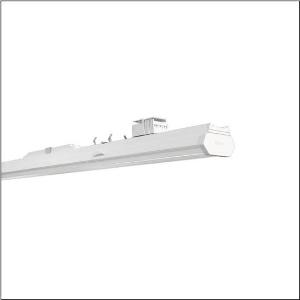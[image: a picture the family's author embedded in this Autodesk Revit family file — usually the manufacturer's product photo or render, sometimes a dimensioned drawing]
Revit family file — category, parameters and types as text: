
# Revit family: licross_r__11_protected_ho_51tp11mn4gxs_ec8e
name_source: partatom
category: Lighting Fixtures
units: mm (PartAtom-declared; Revit-internal decimal feet)

## family parameters
Cut with Voids When Loaded = No
Host = Face
Light Source = No
Part Type = Normal
Room Calculation Point = No
Round Connector Dimension = Use Diameter
Shared = No

## types (1)
- --- (1 x LED, 16070 lm, 87.4 W, 4000K)
    Apparent Load = 87 VA
    CIE Flux Codes = 84 94 98 99 100
    Color Rendering = 80
    Color Temperature = 4000K
    Default Elevation = 1800 mm
    Description = Licross® 11 Protected HO, luminaire insert, of sheet steel, galvanised, coil coated, white, length: 1.500mm, width: 90mm, height: 101mm, LED rated luminous flux: 16.070lm, light colour: 840, control gear: ON/OFF Multilumen, with plug, 3-pole, with phase selection, mains connection: 220..240V, AC, 50/60Hz, rated input power: 87W, halogen-free wiring, primary light control with lens, of plastic, primary optical cover: cover, of PMMA, light emission: direct distribution, primary light characteristic: symmetric, protection rating (complete): IP64, insulation class (complete): insulation class I (protective earthing), certification: CE, ENEC, VDE, UKCA, protection symbol: D if used in an environment with conductive dust loads with corresponding accessories, impact resistance: IK06, permissible ambient temperature for indoor applications: -35..+35°C, corresponds to IFS (International Featured Standards) requirements for safety and quality in the food industry, reducing of maximum allowable ambient temperature of 5°C with ceiling mounting, LABS conformity tested according to VDMA 24364:2018-05, packaging unit: 1 piece
    Height = 92 mm
    Lamp = 1 x LED
    Lamp Light Flux = 16070 lm
    Lamp Power = 87.4 W
    Lamp count = 1
    Length = 1500 mm
    Luminous efficacy = 184 lm/W
    Manufacturer = Siteco
    ModVariant = No
    Model = 51TP11MN4GXS
    Mounting Place = Ceiling
    Mounting Type = Pendant
    Number of Poles = 1
    OnlyDefault = Yes
    Power Factor = 1
    Product Name = Licross® 11 Protected HO
    Product group = luminaire insert
    ProductGroupID = 901
    Protection Class = Protection class I
    Protection Degree = IP 64
    RLX_Detail_Level = 1
    RLX_Emergency_Light_Flux = 0 lm
    RLX_Emergency_Type = 0
    RLX_Emergency_Type_DB = No
    RlxData = <blob elided: 22033 chars, md5=c27a27c4>
    Socket = socket
    Standby Power = 0 W
    System Light Flux = 16070 lm
    System Power = 87 W
    Type Comments = factory setting: luminous flux: 100 % | (A | C | E) | 203 mA
    Type Image = l_1256148.jpg
    URL = http://relux.com
    VarID = @adj_055203
    Voltage = 0 V
    Weight = 0.00 kg
    Width = 88 mm

## geometry (parser evidence)
native form markers: Blend x4, Sweep x11
no freeform markers — native parametric forms only
